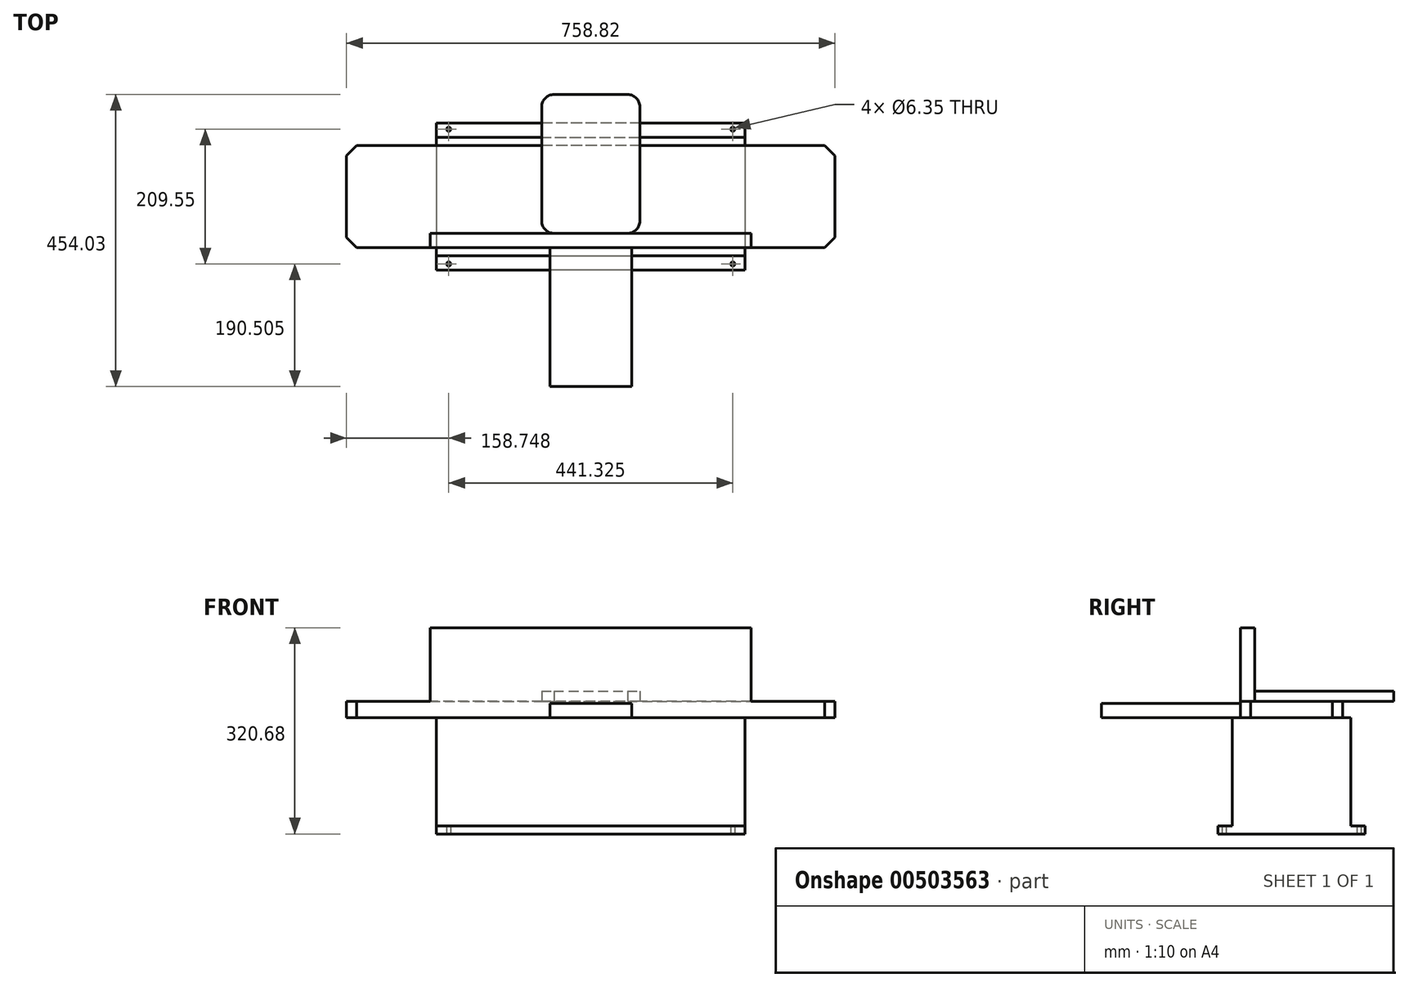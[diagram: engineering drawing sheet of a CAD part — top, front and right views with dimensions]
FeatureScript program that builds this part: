
annotation { "Feature Type Name" : "Feature", "Feature Type Description" : "" }
export const myFeature = defineFeature(function(context is Context, id is Id, definition is map)
    precondition{}
    {
        {
            var Q0;
            Q0=qCreatedBy(makeId("Top.planeOp"),FACE);
            var sketch = newSketch(context, id + "F0", { "sketchPlane" : qUnion([Q0])});
            skLineSegment(sketch, "E0.bottom", {"start": v(239.71, 114.3) * mm, "end": v(-239.71, 114.3) * mm});
            skLineSegment(sketch, "E0.top", {"start": v(239.71, -114.3) * mm, "end": v(-239.71, -114.3) * mm});
            skLineSegment(sketch, "E0.left", {"start": v(239.71, 114.3) * mm, "end": v(239.71, -114.3) * mm});
            skLineSegment(sketch, "E0.right", {"start": v(-239.71, 114.3) * mm, "end": v(-239.71, -114.3) * mm});
            skPoint(sketch, "E0.middle", {"position": v(0, 0) * mm});
            skSolve(sketch);
        }
        {
            var Q0;
            Q0 = qSketchRegion(id + "F0", true);
            extrude(context, id + "F1", {"entities" : qUnion([Q0]), "depth" : 12.7 * mm});
        }
        {
            var Q0;
            Q0=makeQuery(id+"F1.opExtrude","CAP_FACE",FACE,{"disambiguationData":[OSD([sQuery(id+"F0.wireOp",EDGE,"E0.bottom"),sQuery(id+"F0.wireOp",EDGE,"E0.top"),sQuery(id+"F0.wireOp",EDGE,"E0.left"),sQuery(id+"F0.wireOp",EDGE,"E0.right")])],"isStart":true});
            var sketch = newSketch(context, id + "F2", { "sketchPlane" : qUnion([Q0])});
            skCircle(sketch, "E1", {"center": v(220.66, -104.78) * mm, "radius": 3.17 * mm});
            skCircle(sketch, "E2.MirrorC", {"center": v(-220.66, -104.78) * mm, "radius": 3.17 * mm});
            skCircle(sketch, "E3.MirrorC", {"center": v(220.66, 104.78) * mm, "radius": 3.17 * mm});
            skCircle(sketch, "E4.MirrorC", {"center": v(-220.66, 104.78) * mm, "radius": 3.17 * mm});
            skSolve(sketch);
        }
        {
            var Q0;
            Q0 = qSketchRegion(id + "F2", true);
            extrude(context, id + "F3", {"entities" : qUnion([Q0]), "operationType" : NewBodyOperationType.REMOVE, "endBound" : BoundingType.THROUGH_ALL, "oppositeDirection" : true, "depth" : 25.4 * mm});
        }
        {
            var Q0;
            Q0=makeQuery(id+"F1.opExtrude","CAP_FACE",FACE,{"disambiguationData":[OSD([sQuery(id+"F0.wireOp",EDGE,"E0.bottom"),sQuery(id+"F0.wireOp",EDGE,"E0.top"),sQuery(id+"F0.wireOp",EDGE,"E0.left"),sQuery(id+"F0.wireOp",EDGE,"E0.right")])],"isStart":false});
            var sketch = newSketch(context, id + "F4", { "sketchPlane" : qUnion([Q0])});
            skLineSegment(sketch, "E5.bottom", {"start": v(-239.71, 92.07) * mm, "end": v(239.71, 92.07) * mm});
            skLineSegment(sketch, "E5.top", {"start": v(-239.71, -92.08) * mm, "end": v(239.71, -92.08) * mm});
            skLineSegment(sketch, "E5.left", {"start": v(-239.71, 92.07) * mm, "end": v(-239.71, -92.08) * mm});
            skLineSegment(sketch, "E5.right", {"start": v(239.71, 92.08) * mm, "end": v(239.71, -92.08) * mm});
            skLineSegment(sketch, "E6", {"start": v(-239.71, 0) * mm, "end": v(0, 0) * mm, "construction": true});
            skSolve(sketch);
        }
        {
            var Q0;
            Q0 = qSketchRegion(id + "F4", true);
            extrude(context, id + "F5", {"entities" : qUnion([Q0]), "operationType" : NewBodyOperationType.ADD, "depth" : 168.27 * mm});
        }
        {
            var Q0;
            Q0=makeQuery(id+"F5.opExtrude","CAP_FACE",FACE,{"disambiguationData":[OSD([sQuery(id+"F4.wireOp",EDGE,"E5.bottom"),sQuery(id+"F4.wireOp",EDGE,"E5.top"),sQuery(id+"F4.wireOp",EDGE,"E5.left"),sQuery(id+"F4.wireOp",EDGE,"E5.right")])],"isStart":false});
            var sketch = newSketch(context, id + "F6", { "sketchPlane" : qUnion([Q0])});
            skLineSegment(sketch, "E7.bottom", {"start": v(379.41, -79.37) * mm, "end": v(-379.41, -79.37) * mm});
            skLineSegment(sketch, "E7.top", {"start": v(379.41, 79.37) * mm, "end": v(-379.41, 79.37) * mm});
            skLineSegment(sketch, "E7.left", {"start": v(379.41, -79.37) * mm, "end": v(379.41, 79.37) * mm});
            skLineSegment(sketch, "E7.right", {"start": v(-379.41, -79.37) * mm, "end": v(-379.41, 79.37) * mm});
            skPoint(sketch, "E7.middle", {"position": v(0, 0) * mm});
            skSolve(sketch);
        }
        {
            var Q0;
            Q0 = qSketchRegion(id + "F6", true);
            extrude(context, id + "F7", {"entities" : qUnion([Q0]), "operationType" : NewBodyOperationType.ADD, "depth" : 25.4 * mm});
        }
        {
            var Q0;
            Q0=makeQuery(id+"F7.opExtrude","CAP_FACE",FACE,{"disambiguationData":[OSD([sQuery(id+"F6.wireOp",EDGE,"E7.bottom"),sQuery(id+"F6.wireOp",EDGE,"E7.top"),sQuery(id+"F6.wireOp",EDGE,"E7.left"),sQuery(id+"F6.wireOp",EDGE,"E7.right")])],"isStart":false});
            var sketch = newSketch(context, id + "F8", { "sketchPlane" : qUnion([Q0])});
            skLineSegment(sketch, "E8.bottom", {"start": v(-249.24, -79.37) * mm, "end": v(249.24, -79.37) * mm});
            skLineSegment(sketch, "E8.top", {"start": v(-249.24, -57.15) * mm, "end": v(249.24, -57.15) * mm});
            skLineSegment(sketch, "E8.left", {"start": v(-249.24, -79.37) * mm, "end": v(-249.24, -57.15) * mm});
            skLineSegment(sketch, "E8.right", {"start": v(249.24, -79.37) * mm, "end": v(249.24, -57.15) * mm});
            skLineSegment(sketch, "E9", {"start": v(0, -79.37) * mm, "end": v(0, 0) * mm, "construction": true});
            skSolve(sketch);
        }
        {
            var Q0;
            Q0 = qSketchRegion(id + "F8", true);
            extrude(context, id + "F9", {"entities" : qUnion([Q0]), "operationType" : NewBodyOperationType.ADD, "depth" : 114.3 * mm});
        }
        {
            var Q0;
            Q0=makeQuery(id+"F9.boolean.opBoolean","MERGE",FACE,{"derivedFrom":[makeQuery(id+"F7.opExtrude","SWEPT_FACE",FACE,{"disambiguationData":[OSD([sQuery(id+"F6.wireOp",EDGE,"E7.bottom")])]}),makeQuery(id+"F9.opExtrude","SWEPT_FACE",FACE,{"disambiguationData":[OSD([sQuery(id+"F8.wireOp",EDGE,"E8.bottom")])]})]});
            var sketch = newSketch(context, id + "F10", { "sketchPlane" : qUnion([Q0])});
            skLineSegment(sketch, "E10.bottom", {"start": v(63.5, 180.97) * mm, "end": v(-63.5, 180.97) * mm});
            skLineSegment(sketch, "E10.top", {"start": v(63.5, 203.2) * mm, "end": v(-63.5, 203.2) * mm});
            skLineSegment(sketch, "E10.left", {"start": v(63.5, 180.97) * mm, "end": v(63.5, 203.2) * mm});
            skLineSegment(sketch, "E10.right", {"start": v(-63.5, 180.97) * mm, "end": v(-63.5, 203.2) * mm});
            skPoint(sketch, "E10.middle", {"position": v(0, 192.09) * mm});
            skSolve(sketch);
        }
        {
            var Q0;
            Q0 = qSketchRegion(id + "F10", true);
            extrude(context, id + "F11", {"entities" : qUnion([Q0]), "operationType" : NewBodyOperationType.ADD, "depth" : 215.9 * mm});
        }
        {
            var Q0;
            Q0=makeQuery(id+"F7.opExtrude","SWEPT_EDGE",EDGE,{"disambiguationData":[OSD([sQuery(id+"F6.wireOp",EDGE,"E7.top"),sQuery(id+"F6.wireOp",EDGE,"E7.right")])]});
            var Q1;
            Q1=makeQuery(id+"F7.opExtrude","SWEPT_EDGE",EDGE,{"disambiguationData":[OSD([sQuery(id+"F6.wireOp",EDGE,"E7.bottom"),sQuery(id+"F6.wireOp",EDGE,"E7.right")])]});
            var Q2;
            Q2=makeQuery(id+"F7.opExtrude","SWEPT_EDGE",EDGE,{"disambiguationData":[OSD([sQuery(id+"F6.wireOp",EDGE,"E7.bottom"),sQuery(id+"F6.wireOp",EDGE,"E7.left")])]});
            var Q3;
            Q3=makeQuery(id+"F7.opExtrude","SWEPT_EDGE",EDGE,{"disambiguationData":[OSD([sQuery(id+"F6.wireOp",EDGE,"E7.top"),sQuery(id+"F6.wireOp",EDGE,"E7.left")])]});
            chamfer(context, id + "F12", {"entities" : qUnion([Q0, Q1, Q2, Q3]), "width" : 15.88 * mm, "tangentPropagation" : true});
        }
        {
            var Q0;
            Q0=makeQuery(id+"F7.opExtrude","CAP_FACE",FACE,{"disambiguationData":[OSD([sQuery(id+"F6.wireOp",EDGE,"E7.bottom"),sQuery(id+"F6.wireOp",EDGE,"E7.top"),sQuery(id+"F6.wireOp",EDGE,"E7.left"),sQuery(id+"F6.wireOp",EDGE,"E7.right")])],"isStart":false});
            var sketch = newSketch(context, id + "F13", { "sketchPlane" : qUnion([Q0])});
            skLineSegment(sketch, "E11.bottom", {"start": v(-57.15, -57.15) * mm, "end": v(57.15, -57.15) * mm});
            skLineSegment(sketch, "E11.top", {"start": v(-57.15, 158.75) * mm, "end": v(57.15, 158.75) * mm});
            skLineSegment(sketch, "E11.left", {"start": v(-76.2, -38.1) * mm, "end": v(-76.2, 139.7) * mm});
            skLineSegment(sketch, "E11.right", {"start": v(76.2, -38.1) * mm, "end": v(76.2, 139.7) * mm});
            skLineSegment(sketch, "E12", {"start": v(0, -57.15) * mm, "end": v(0, 73.03) * mm, "construction": true});
            skPoint(sketch, "E13.visualSharp", {"position": v(-76.2, 158.75) * mm});
            skArc(sketch, "E13.filletArc", {"start": v(-57.15, 158.75) * mm, "mid": v(-70.62, 153.17) * mm, "end": v(-76.2, 139.7) * mm});
            skPoint(sketch, "E14.visualSharp", {"position": v(76.2, 158.75) * mm});
            skArc(sketch, "E14.filletArc", {"start": v(76.2, 139.7) * mm, "mid": v(70.62, 153.17) * mm, "end": v(57.15, 158.75) * mm});
            skPoint(sketch, "E15.visualSharp", {"position": v(76.2, -57.15) * mm});
            skArc(sketch, "E15.filletArc", {"start": v(57.15, -57.15) * mm, "mid": v(70.62, -51.57) * mm, "end": v(76.2, -38.1) * mm});
            skPoint(sketch, "E16.visualSharp", {"position": v(-76.2, -57.15) * mm});
            skArc(sketch, "E16.filletArc", {"start": v(-76.2, -38.1) * mm, "mid": v(-70.62, -51.57) * mm, "end": v(-57.15, -57.15) * mm});
            skSolve(sketch);
        }
        {
            var Q0;
            Q0 = qSketchRegion(id + "F13", true);
            extrude(context, id + "F14", {"entities" : qUnion([Q0]), "operationType" : NewBodyOperationType.ADD, "depth" : 15.88 * mm});
        }
    });
